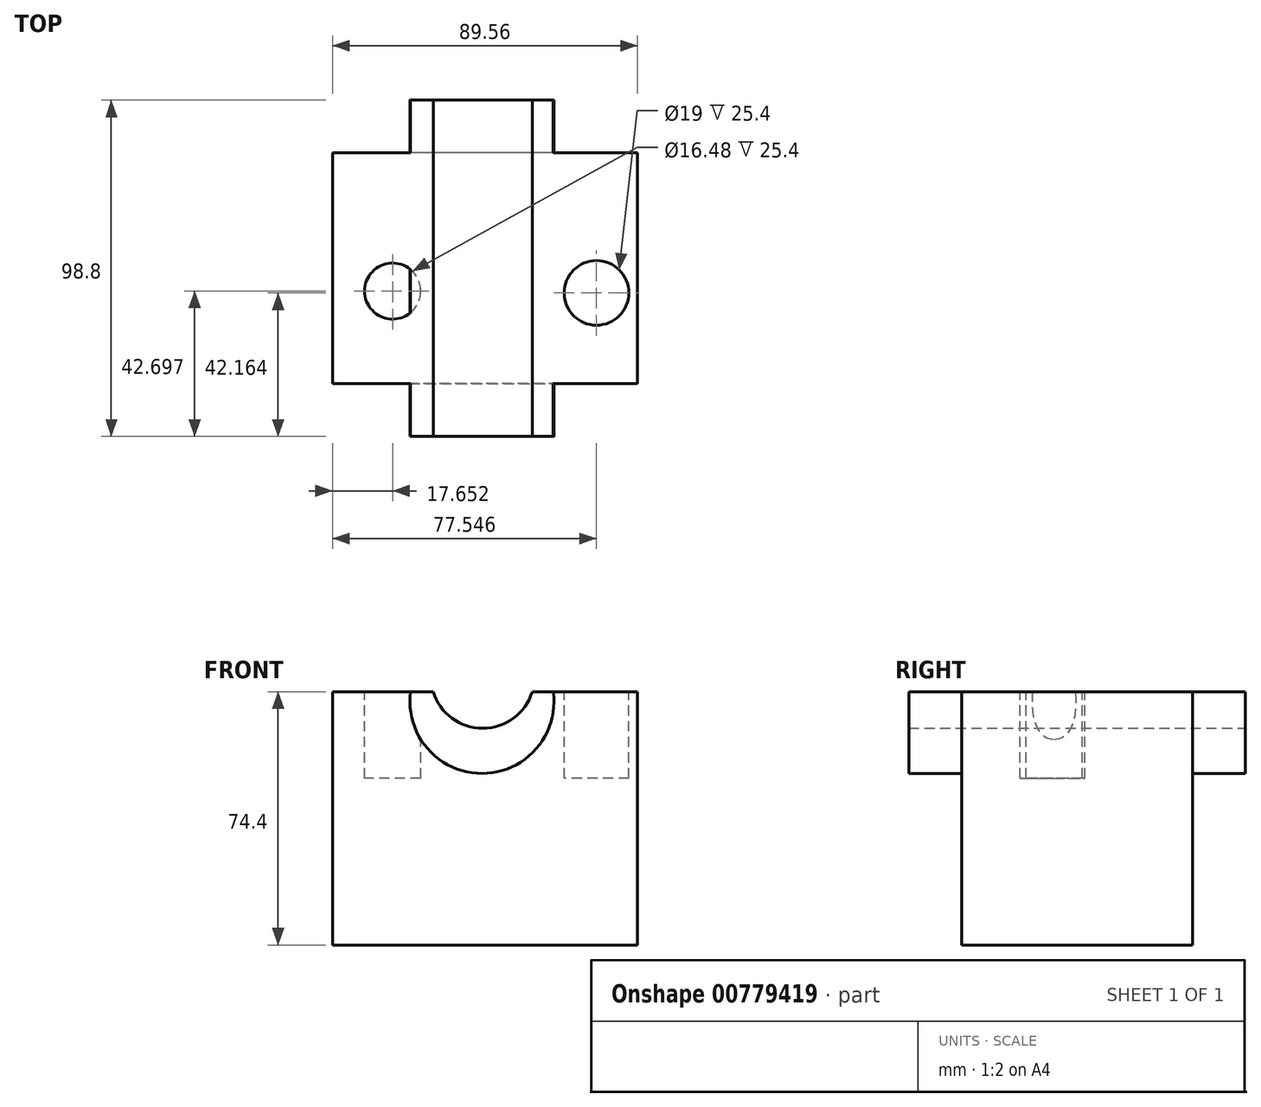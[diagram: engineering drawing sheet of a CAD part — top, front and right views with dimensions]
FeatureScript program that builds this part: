
annotation { "Feature Type Name" : "Feature", "Feature Type Description" : "" }
export const myFeature = defineFeature(function(context is Context, id is Id, definition is map)
    precondition{}
    {
        {
            var Q0;
            Q0=qCreatedBy(makeId("Front.planeOp"),FACE);
            var sketch = newSketch(context, id + "F0", { "sketchPlane" : qUnion([Q0])});
            skLineSegment(sketch, "E0.bottom", {"start": v(44.78, -37.2) * mm, "end": v(-44.78, -37.2) * mm});
            skLineSegment(sketch, "E0.top", {"start": v(44.78, 37.2) * mm, "end": v(-44.78, 37.2) * mm});
            skLineSegment(sketch, "E0.left", {"start": v(44.78, -37.2) * mm, "end": v(44.78, 37.2) * mm});
            skLineSegment(sketch, "E0.right", {"start": v(-44.78, -37.2) * mm, "end": v(-44.78, 37.2) * mm});
            skPoint(sketch, "E0.middle", {"position": v(0, 0) * mm});
            skArc(sketch, "E1", {"start": v(-15.22, 37.2) * mm, "mid": v(-0.66, 26.49) * mm, "end": v(13.9, 37.2) * mm});
            skSolve(sketch);
        }
        {
            var Q0;
            Q0=makeQuery(id+"F0.imprint","IMPRINT",FACE,{"disambiguationData":[TD([[makeQuery(id+"F0.imprint","IMPRINT",EDGE,{"derivedFrom":sQuery(id+"F0.wireOp",EDGE,"E0.bottom")}),-1.0]])]});
            extrude(context, id + "F1", {"entities" : qUnion([Q0]), "depth" : 42.42 * mm, "offsetDistance" : 25.4 * mm});
        }
        {
            var Q0;
            Q0=makeQuery(id+"F1.opExtrude","CAP_FACE",FACE,{"disambiguationData":[OSD([sQuery(id+"F0.wireOp",EDGE,"E0.bottom"),sQuery(id+"F0.wireOp",EDGE,"E0.top"),sQuery(id+"F0.wireOp",EDGE,"E0.left"),sQuery(id+"F0.wireOp",EDGE,"E0.right"),sQuery(id+"F0.wireOp",EDGE,"E1")])],"isStart":true});
            extrude(context, id + "F2", {"entities" : qUnion([Q0]), "operationType" : NewBodyOperationType.ADD, "depth" : 25.4 * mm, "offsetDistance" : 25.4 * mm});
        }
        {
            var Q0;
            {var subQ0=sQuery(id+"F0.wireOp",EDGE,"E0.top");var subQ1=makeQuery(id+"F0.imprint","IMPRINT",EDGE,{"disambiguationData":[TD([[makeQuery(id+"F0.imprint","INTERSECT",VERTEX,{"derivedFrom":[subQ0,sQuery(id+"F0.wireOp",EDGE,"E0.right")]}),1.0]])],"derivedFrom":subQ0});Q0=makeQuery(id+"F2.boolean.opBoolean","MERGE",FACE,{"derivedFrom":[makeQuery(id+"F1.opExtrude","SWEPT_FACE",FACE,{"disambiguationData":[OSD([subQ0]),TDD([subQ1])]}),makeQuery(id+"F2.opExtrude","SWEPT_FACE",FACE,{"disambiguationData":[OSD([subQ0]),TDD([makeQuery(id+"F1.opExtrude","CAP_EDGE",EDGE,{"disambiguationData":[OSD([subQ0]),TDD([subQ1])],"isStart":true})])]})]});}
            var sketch = newSketch(context, id + "F3", { "sketchPlane" : qUnion([Q0])});
            skCircle(sketch, "E2", {"center": v(-27.13, -15.21) * mm, "radius": 8.24 * mm});
            skCircle(sketch, "E3", {"center": v(32.77, -15.75) * mm, "radius": 9.5 * mm});
            skSolve(sketch);
        }
        {
            var Q0;
            Q0=makeQuery(id+"F3.imprint","IMPRINT",FACE,{"disambiguationData":[TD([[makeQuery(id+"F3.imprint","IMPRINT",EDGE,{"derivedFrom":sQuery(id+"F3.wireOp",EDGE,"E2")}),1.0]])]});
            var Q1;
            Q1=makeQuery(id+"F3.imprint","IMPRINT",FACE,{"disambiguationData":[TD([[makeQuery(id+"F3.imprint","IMPRINT",EDGE,{"derivedFrom":sQuery(id+"F3.wireOp",EDGE,"E3")}),1.0]])]});
            extrude(context, id + "F4", {"entities" : qUnion([Q0, Q1]), "operationType" : NewBodyOperationType.REMOVE, "oppositeDirection" : true, "depth" : 25.4 * mm, "offsetDistance" : 25.4 * mm});
        }
        {
            var Q0;
            Q0=makeQuery(id+"F2.opExtrude","CAP_FACE",FACE,{"disambiguationData":[OSD([sQuery(id+"F0.wireOp",EDGE,"E0.bottom"),sQuery(id+"F0.wireOp",EDGE,"E0.top"),sQuery(id+"F0.wireOp",EDGE,"E0.left"),sQuery(id+"F0.wireOp",EDGE,"E0.right"),sQuery(id+"F0.wireOp",EDGE,"E1")])],"isStart":false});
            var sketch = newSketch(context, id + "F5", { "sketchPlane" : qUnion([Q0])});
            skArc(sketch, "E4", {"start": v(-20.08, 37.2) * mm, "mid": v(0.9, 13.2) * mm, "end": v(21.86, 37.2) * mm});
            skSolve(sketch);
        }
        {
            var Q0;
            {var subQ0=sQuery(id+"F5.wireOp",EDGE,"E4");Q0=makeQuery(id+"F5.imprint","IMPRINT",FACE,{"disambiguationData":[TD([[makeQuery(id+"F5.imprint","IMPRINT",EDGE,{"derivedFrom":subQ0}),1.0]])]});}
            extrude(context, id + "F6", {"entities" : qUnion([Q0]), "operationType" : NewBodyOperationType.ADD, "depth" : 15.5 * mm, "offsetDistance" : 25.4 * mm});
        }
        {
            var Q0;
            Q0=makeQuery(id+"F6.opExtrude","CAP_FACE",FACE,{"disambiguationData":[OSD([sQuery(id+"F0.wireOp",EDGE,"E0.top"),sQuery(id+"F0.wireOp",EDGE,"E1"),sQuery(id+"F5.wireOp",EDGE,"E4")])],"isStart":false});
            extrude(context, id + "F7", {"entities" : qUnion([Q0]), "operationType" : NewBodyOperationType.ADD, "oppositeDirection" : true, "depth" : 98.8 * mm, "offsetDistance" : 25.4 * mm});
        }
    });
